# Revit family: Bath-Freestanding-KOHLER-Veil-K-8331_1
name_source: partatom
category: Plumbing Fixtures
units: mm (PartAtom-declared; Revit-internal decimal feet)

## family parameters
Cut with Voids When Loaded = No
Host = Face
Maintain Annotation Orientation = No
OmniClass Number = 23.31.15.00
OmniClass Title = Bathtubs
Part Type = Normal
Room Calculation Point = No
Round Connector Dimension = Use Diameter
Shared = No

## types (3) — shared parameters
ADA Compliant = No
Assembly Code = D2010500
CW Connection = No
Cold Water Inlet = Cold Water Inlet
Date Modified = 05/11/2022
Default Elevation = 0"
Description = 65-7/16 inch x 36-7/16 inch freestanding bath with center toe-tap drain
Drain Included = Yes
Finish = Kohler-Lithocast-0-White
HW Connection = No
Height = 24 3/8"
Hot Water Inlet = Hot Water Inlet
Length = 36 15/16"
Manufacturer = Kohler Co.
Master Format 2014 = 22 41 19
Master Format 2014 Name = Residential Bathtubs
Material = Lithocast Gloss
Model = K-8331-0
Product Documentation Link = https://www.us.kohler.com
Product Name = Veil
Product Page URL = http://www.us.kohler.com
URL = http://www.us.kohler.com
Vent Connection = No
Waste Connection = Yes
Waste Water Outlet = Waste Water Outlet
WaterSense Certified = No
Width = 65 3/8"

## per-type parameters (varying)
| type | Secondary Finish |
| White Drain, 0-White | Kohler-Metal-0-White |
| Vibrant Brushed Nickel Drain, 0-White | Kohler-Metal-BN-Vibrant_Brushed_Nickel |
| Polished Chrome Drain, 0-White | Kohler-Metal-CP-Polished_Chrome |

## geometry (parser evidence)
native form markers: Sweep x3
no freeform markers — native parametric forms only
